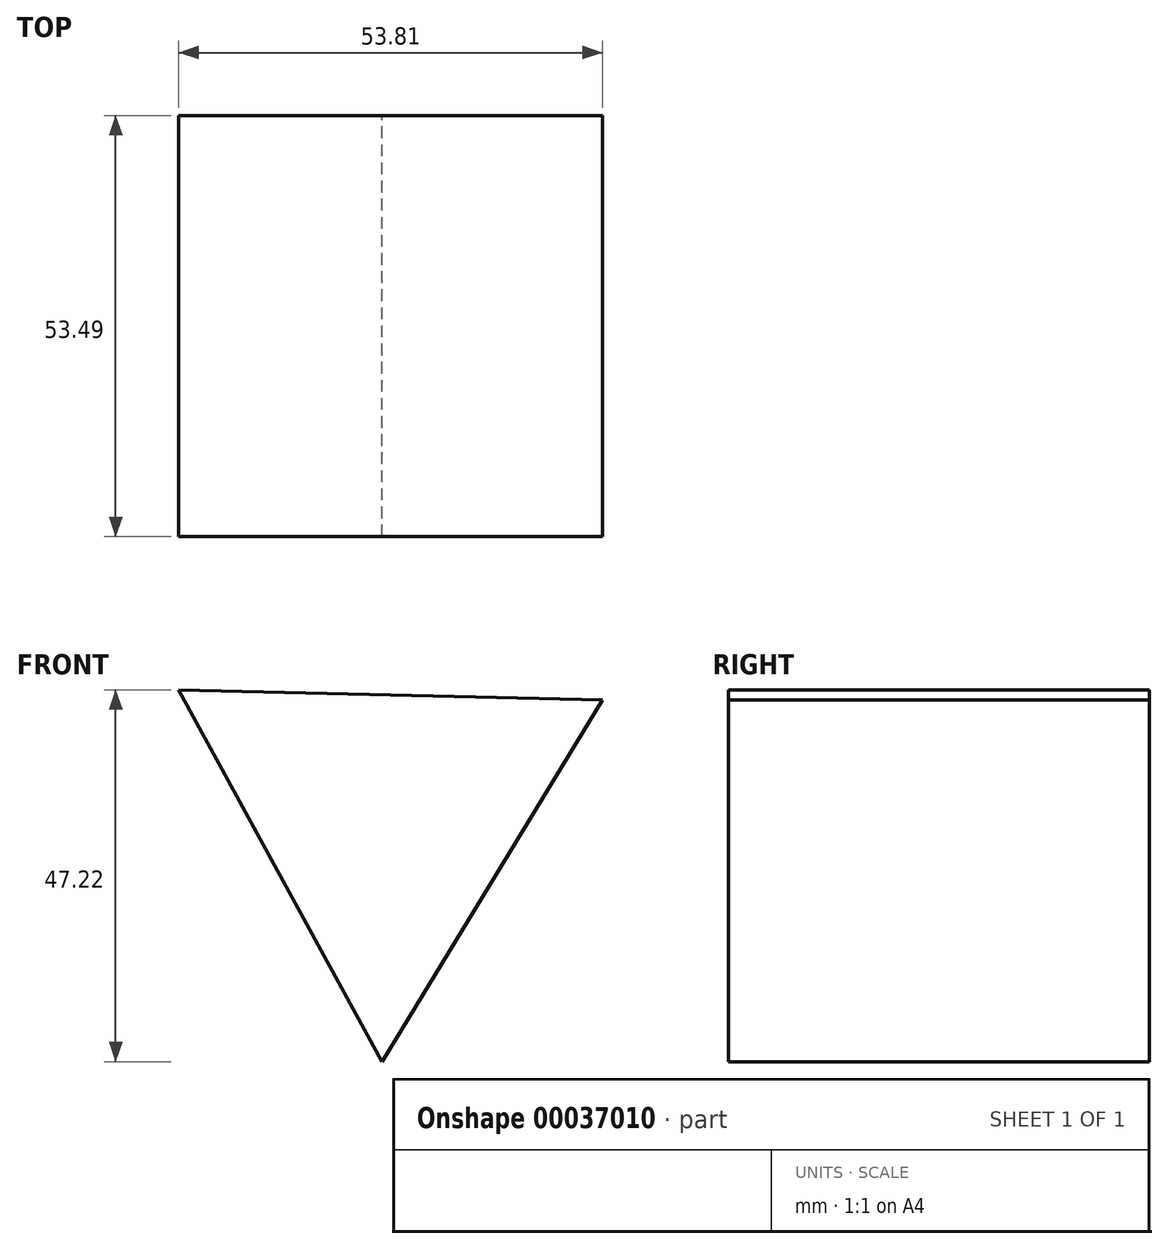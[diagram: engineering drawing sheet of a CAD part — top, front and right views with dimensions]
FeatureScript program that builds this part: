
annotation { "Feature Type Name" : "Feature", "Feature Type Description" : "" }
export const myFeature = defineFeature(function(context is Context, id is Id, definition is map)
    precondition{}
    {
        {
            var Q0;
            Q0=qCreatedBy(makeId("Front.planeOp"),FACE);
            var sketch = newSketch(context, id + "F0", { "sketchPlane" : qUnion([Q0])});
            skCircle(sketch, "E0.cCircle", {"center": v(22.73, 22.84) * mm, "radius": 15.54 * mm, "construction": true});
            skLineSegment(sketch, "E0.0", {"start": v(22, -8.23) * mm, "end": v(-3.82, 39) * mm});
            skLineSegment(sketch, "E0.1", {"start": v(-3.82, 39) * mm, "end": v(50, 37.75) * mm});
            skLineSegment(sketch, "E0.2", {"start": v(50, 37.75) * mm, "end": v(22, -8.23) * mm});
            skPoint(sketch, "E0.0.midPoint", {"position": v(9.1, 15.38) * mm});
            skSolve(sketch);
        }
        {
            var Q0;
            Q0=makeQuery(id+"F0.imprint","IMPRINT",FACE,{"disambiguationData":[TD([[makeQuery(id+"F0.imprint","IMPRINT",EDGE,{"derivedFrom":sQuery(id+"F0.wireOp",EDGE,"E0.0")}),-1.0]])]});
            extrude(context, id + "F1", {"entities" : qUnion([Q0]), "depth" : 53.5 * mm});
        }
    });
